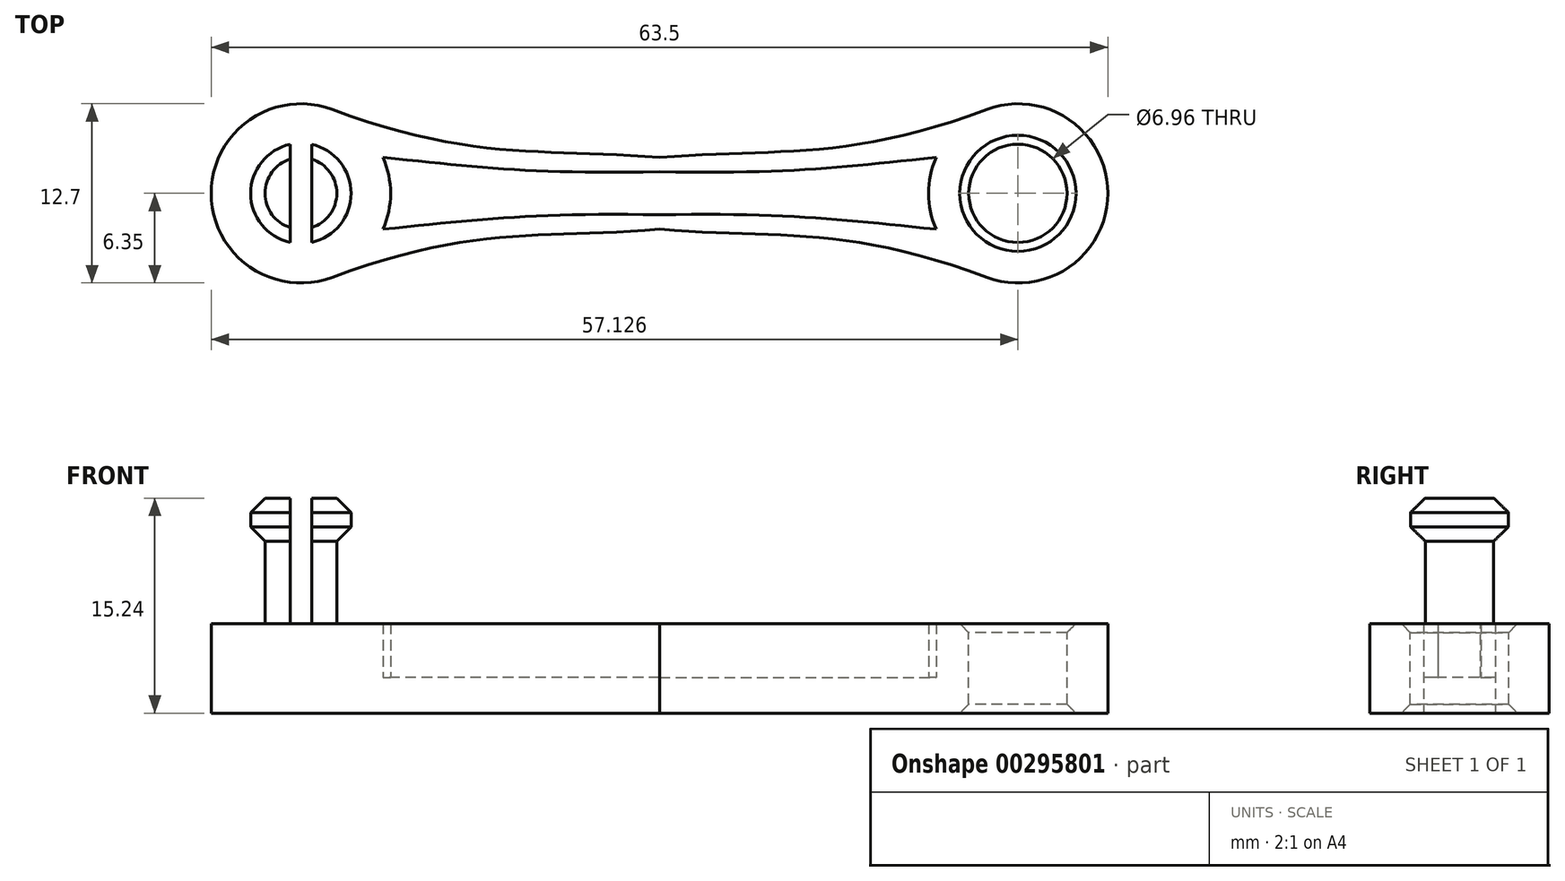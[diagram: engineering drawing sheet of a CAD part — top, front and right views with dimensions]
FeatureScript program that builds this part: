
annotation { "Feature Type Name" : "Feature", "Feature Type Description" : "" }
export const myFeature = defineFeature(function(context is Context, id is Id, definition is map)
    precondition{}
    {
        {
            var Q0;
            Q0=qCreatedBy(makeId("Top.planeOp"),FACE);
            var sketch = newSketch(context, id + "F0", { "sketchPlane" : qUnion([Q0])});
            skLineSegment(sketch, "E0.left", {"start": v(-25.42, 6.35) * mm, "end": v(-25.38, -6.35) * mm, "construction": true});
            skLineSegment(sketch, "E0.right", {"start": v(25.38, 6.35) * mm, "end": v(25.42, -6.35) * mm, "construction": true});
            skPoint(sketch, "E0.middle", {"position": v(0, 0) * mm});
            skCircle(sketch, "E1", {"center": v(-25.4, 0) * mm, "radius": 6.35 * mm});
            skCircle(sketch, "E2", {"center": v(25.4, 0) * mm, "radius": 6.35 * mm});
            skLineSegment(sketch, "E3", {"start": v(0, 0) * mm, "end": v(0, 1.52) * mm, "construction": true});
            skLineSegment(sketch, "E4", {"start": v(0, 1.52) * mm, "end": v(0, 2.54) * mm, "construction": true});
            skFitSpline(sketch, "E5", {"points": [v(0, 1.52) * mm, v(-19.58, 2.54) * mm], "startDerivative": vector(-27.23, -0.5) * mm, "endDerivative": vector(-20.14, 2.02) * mm});
            skFitSpline(sketch, "E6.MirrorCS", {"points": [v(0, 1.52) * mm, v(19.58, 2.54) * mm], "startDerivative": vector(27.23, -0.5) * mm, "endDerivative": vector(20.14, 2.02) * mm});
            skFitSpline(sketch, "E7.MirrorCS", {"points": [v(0, -1.52) * mm, v(19.58, -2.54) * mm], "startDerivative": vector(27.23, 0.5) * mm, "endDerivative": vector(20.14, -2.02) * mm});
            skFitSpline(sketch, "E8.MirrorCS", {"points": [v(0, -1.52) * mm, v(-19.58, -2.54) * mm], "startDerivative": vector(-27.23, 0.5) * mm, "endDerivative": vector(-20.14, -2.02) * mm});
            skFitSpline(sketch, "E9", {"points": [v(0, 2.54) * mm, v(-23.18, 5.95) * mm], "startDerivative": vector(-24.38, 2.12) * mm, "endDerivative": vector(-30.2, 11.29) * mm});
            skFitSpline(sketch, "E10.MirrorCS", {"points": [v(0, 2.54) * mm, v(23.18, 5.95) * mm], "startDerivative": vector(24.38, 2.12) * mm, "endDerivative": vector(30.2, 11.29) * mm});
            skFitSpline(sketch, "E11.MirrorCS", {"points": [v(0, -2.54) * mm, v(-23.18, -5.95) * mm], "startDerivative": vector(-24.38, -2.12) * mm, "endDerivative": vector(-30.2, -11.29) * mm});
            skFitSpline(sketch, "E12.MirrorCS", {"points": [v(0, -2.54) * mm, v(23.18, -5.95) * mm], "startDerivative": vector(24.38, -2.12) * mm, "endDerivative": vector(30.2, -11.29) * mm});
            skSolve(sketch);
        }
        {
            var Q0;
            Q0=qCreatedBy(makeId("Front.planeOp"),FACE);
            var sketch = newSketch(context, id + "F1", { "sketchPlane" : qUnion([Q0])});
            skPoint(sketch, "E13.0", {"position": v(25.38, 0) * mm});
            skLineSegment(sketch, "E14", {"start": v(25.38, 0) * mm, "end": v(25.38, 6.35) * mm});
            skLineSegment(sketch, "E15.bottom", {"start": v(28.86, 5.72) * mm, "end": v(21.9, 5.72) * mm, "construction": true});
            skLineSegment(sketch, "E15.top", {"start": v(28.86, 0.64) * mm, "end": v(21.9, 0.64) * mm, "construction": true});
            skLineSegment(sketch, "E15.left", {"start": v(28.86, 5.72) * mm, "end": v(28.86, 0.64) * mm});
            skLineSegment(sketch, "E15.right", {"start": v(21.9, 5.72) * mm, "end": v(21.9, 0.64) * mm});
            skPoint(sketch, "E15.middle", {"position": v(25.38, 3.18) * mm});
            skLineSegment(sketch, "E16.bottom", {"start": v(29.5, 0) * mm, "end": v(21.26, 0) * mm});
            skLineSegment(sketch, "E16.top", {"start": v(29.5, 6.35) * mm, "end": v(21.26, 6.35) * mm});
            skLineSegment(sketch, "E16.left", {"start": v(29.5, 0) * mm, "end": v(29.5, 6.35) * mm, "construction": true});
            skLineSegment(sketch, "E16.right", {"start": v(21.26, 0) * mm, "end": v(21.26, 6.35) * mm, "construction": true});
            skLineSegment(sketch, "E17", {"start": v(28.86, 5.72) * mm, "end": v(29.5, 6.35) * mm});
            skLineSegment(sketch, "E18", {"start": v(21.9, 5.72) * mm, "end": v(21.26, 6.35) * mm});
            skLineSegment(sketch, "E19", {"start": v(21.9, 0.64) * mm, "end": v(21.26, 0) * mm});
            skLineSegment(sketch, "E20", {"start": v(28.86, 0.64) * mm, "end": v(29.5, 0) * mm});
            skPoint(sketch, "E21.0", {"position": v(-25.4, 0) * mm});
            skLineSegment(sketch, "E22", {"start": v(-25.4, 0) * mm, "end": v(-25.4, 6.35) * mm, "construction": true});
            skLineSegment(sketch, "E23", {"start": v(-25.4, 6.35) * mm, "end": v(-25.4, 15.24) * mm});
            skLineSegment(sketch, "E24.bottom", {"start": v(-22.86, 15.24) * mm, "end": v(-27.94, 15.24) * mm});
            skLineSegment(sketch, "E24.top", {"start": v(-22.86, 6.35) * mm, "end": v(-27.94, 6.35) * mm});
            skLineSegment(sketch, "E24.left", {"start": v(-22.86, 15.24) * mm, "end": v(-22.86, 6.35) * mm});
            skLineSegment(sketch, "E24.right", {"start": v(-27.94, 15.24) * mm, "end": v(-27.94, 6.35) * mm});
            skPoint(sketch, "E24.middle", {"position": v(-25.4, 10.8) * mm});
            skLineSegment(sketch, "E25.bottom", {"start": v(-21.84, 15.24) * mm, "end": v(-28.96, 15.24) * mm});
            skLineSegment(sketch, "E25.top", {"start": v(-21.84, 12.2) * mm, "end": v(-28.96, 12.2) * mm});
            skLineSegment(sketch, "E25.left", {"start": v(-21.84, 15.24) * mm, "end": v(-21.84, 12.2) * mm});
            skLineSegment(sketch, "E25.right", {"start": v(-28.96, 15.24) * mm, "end": v(-28.96, 12.2) * mm});
            skPoint(sketch, "E25.middle", {"position": v(-25.4, 13.72) * mm});
            skLineSegment(sketch, "E26", {"start": v(-21.84, 14.22) * mm, "end": v(-22.86, 15.24) * mm});
            skLineSegment(sketch, "E27", {"start": v(-21.84, 13.2) * mm, "end": v(-22.86, 12.2) * mm});
            skLineSegment(sketch, "E28", {"start": v(-27.94, 15.24) * mm, "end": v(-28.96, 14.22) * mm});
            skLineSegment(sketch, "E29", {"start": v(-27.94, 12.2) * mm, "end": v(-28.96, 13.2) * mm});
            skLineSegment(sketch, "E30.bottom", {"start": v(-24.64, 15.24) * mm, "end": v(-26.16, 15.24) * mm});
            skLineSegment(sketch, "E30.top", {"start": v(-24.64, 6.35) * mm, "end": v(-26.16, 6.35) * mm});
            skLineSegment(sketch, "E30.left", {"start": v(-24.64, 15.24) * mm, "end": v(-24.64, 6.35) * mm});
            skLineSegment(sketch, "E30.right", {"start": v(-26.16, 15.24) * mm, "end": v(-26.16, 6.35) * mm});
            skSolve(sketch);
        }
        {
            var Q0;
            {var subQ0=sQuery(id+"F0.wireOp",EDGE,"E2");var subQ1=makeQuery(id+"F0.imprint","INTERSECT",VERTEX,{"derivedFrom":[sQuery(id+"F0.wireOp",EDGE,"E0.bottom"),subQ0]});Q0=makeQuery(id+"F0.imprint","IMPRINT",FACE,{"disambiguationData":[TD([[makeQuery(id+"F0.imprint","IMPRINT",EDGE,{"disambiguationData":[TD([[subQ1,-1.0]])],"derivedFrom":subQ0}),1.0]])]});}
            var Q1;
            {var subQ0=sQuery(id+"F0.wireOp",EDGE,"E1");var subQ1=makeQuery(id+"F0.imprint","INTERSECT",VERTEX,{"derivedFrom":[sQuery(id+"F0.wireOp",EDGE,"E0.bottom"),subQ0]});Q1=makeQuery(id+"F0.imprint","IMPRINT",FACE,{"disambiguationData":[TD([[makeQuery(id+"F0.imprint","IMPRINT",EDGE,{"disambiguationData":[TD([[subQ1,-1.0]])],"derivedFrom":subQ0}),1.0]])]});}
            var Q2;
            {var subQ8=sQuery(id+"F0.wireOp",EDGE,"E5");Q2=makeQuery(id+"F0.imprint","IMPRINT",FACE,{"disambiguationData":[TD([[makeQuery(id+"F0.imprint","IMPRINT",EDGE,{"derivedFrom":subQ8}),-1.0]])]});}
            var Q3;
            {var subQ7=sQuery(id+"F0.wireOp",EDGE,"E7.MirrorCS");Q3=makeQuery(id+"F0.imprint","IMPRINT",FACE,{"disambiguationData":[TD([[makeQuery(id+"F0.imprint","IMPRINT",EDGE,{"derivedFrom":subQ7}),-1.0]])]});}
            extrude(context, id + "F2", {"entities" : qUnion([Q0, Q1, Q2, Q3]), "depth" : 6.35 * mm});
        }
        {
            var Q0;
            {var subQ1=sQuery(id+"F1.wireOp",EDGE,"E14");Q0=makeQuery(id+"F1.imprint","IMPRINT",FACE,{"disambiguationData":[TD([[makeQuery(id+"F1.imprint","IMPRINT",EDGE,{"derivedFrom":subQ1}),-1.0]])]});}
            var Q1;
            Q1=sQuery(id+"F1.wireOp",EDGE,"E14");
            revolve(context, id + "F3", {"operationType" : NewBodyOperationType.REMOVE, "entities" : qUnion([Q0]), "axis" : qUnion([Q1]), "revolveType" : RevolveType.FULL, "oppositeDirection" : true});
        }
        {
            var Q0;
            {var subQ0=sQuery(id+"F1.wireOp",EDGE,"E26");Q0=makeQuery(id+"F1.imprint","IMPRINT",FACE,{"disambiguationData":[TD([[makeQuery(id+"F1.imprint","IMPRINT",EDGE,{"derivedFrom":subQ0}),1.0]])]});}
            var Q1;
            {var subQ3=sQuery(id+"F1.wireOp",EDGE,"E25.top");var subQ5=sQuery(id+"F1.wireOp",EDGE,"E30.left");var subQ7=makeQuery(id+"F1.imprint","INTERSECT",VERTEX,{"derivedFrom":[subQ3,subQ5]});Q1=makeQuery(id+"F1.imprint","IMPRINT",FACE,{"disambiguationData":[TD([[makeQuery(id+"F1.imprint","IMPRINT",EDGE,{"disambiguationData":[TD([[subQ7,1.0]])],"derivedFrom":subQ3}),-1.0]])]});}
            var Q2;
            {var subQ3=sQuery(id+"F1.wireOp",EDGE,"E25.top");var subQ5=sQuery(id+"F1.wireOp",EDGE,"E30.right");var subQ6=makeQuery(id+"F1.imprint","INTERSECT",VERTEX,{"derivedFrom":[subQ3,subQ5]});Q2=makeQuery(id+"F1.imprint","IMPRINT",FACE,{"disambiguationData":[TD([[makeQuery(id+"F1.imprint","IMPRINT",EDGE,{"disambiguationData":[TD([[subQ6,-1.0]])],"derivedFrom":subQ3}),-1.0]])]});}
            var Q3;
            {var subQ0=sQuery(id+"F1.wireOp",EDGE,"E28");Q3=makeQuery(id+"F1.imprint","IMPRINT",FACE,{"disambiguationData":[TD([[makeQuery(id+"F1.imprint","IMPRINT",EDGE,{"derivedFrom":subQ0}),1.0]])]});}
            var Q4;
            {var subQ0=sQuery(id+"F1.wireOp",EDGE,"E24.right");var subQ1=sQuery(id+"F1.wireOp",EDGE,"E24.top");var subQ2=makeQuery(id+"F1.imprint","INTERSECT",VERTEX,{"derivedFrom":[subQ1,subQ0]});Q4=makeQuery(id+"F1.imprint","IMPRINT",FACE,{"disambiguationData":[TD([[makeQuery(id+"F1.imprint","IMPRINT",EDGE,{"disambiguationData":[TD([[subQ2,1.0]])],"derivedFrom":subQ1}),-1.0]])]});}
            var Q5;
            {var subQ0=sQuery(id+"F1.wireOp",EDGE,"E24.left");var subQ1=sQuery(id+"F1.wireOp",EDGE,"E24.top");var subQ2=makeQuery(id+"F1.imprint","INTERSECT",VERTEX,{"derivedFrom":[subQ1,subQ0]});Q5=makeQuery(id+"F1.imprint","IMPRINT",FACE,{"disambiguationData":[TD([[makeQuery(id+"F1.imprint","IMPRINT",EDGE,{"disambiguationData":[TD([[subQ2,-1.0]])],"derivedFrom":subQ1}),-1.0]])]});}
            var Q6;
            Q6=sQuery(id+"F1.wireOp",EDGE,"E23");
            revolve(context, id + "F4", {"operationType" : NewBodyOperationType.ADD, "entities" : qUnion([Q0, Q1, Q2, Q3, Q4, Q5]), "axis" : qUnion([Q6]), "revolveType" : RevolveType.FULL});
        }
        {
            var Q0;
            {var subQ0=sQuery(id+"F1.wireOp",EDGE,"E30.bottom");var subQ1=sQuery(id+"F1.wireOp",EDGE,"E23");var subQ2=makeQuery(id+"F1.imprint","INTERSECT",VERTEX,{"derivedFrom":[subQ1,subQ0]});Q0=makeQuery(id+"F1.imprint","IMPRINT",FACE,{"disambiguationData":[TD([[makeQuery(id+"F1.imprint","IMPRINT",EDGE,{"disambiguationData":[TD([[subQ2,1.0]])],"derivedFrom":subQ1}),-1.0]])]});}
            var Q1;
            {var subQ0=sQuery(id+"F1.wireOp",EDGE,"E30.bottom");var subQ1=sQuery(id+"F1.wireOp",EDGE,"E23");var subQ2=makeQuery(id+"F1.imprint","INTERSECT",VERTEX,{"derivedFrom":[subQ1,subQ0]});Q1=makeQuery(id+"F1.imprint","IMPRINT",FACE,{"disambiguationData":[TD([[makeQuery(id+"F1.imprint","IMPRINT",EDGE,{"disambiguationData":[TD([[subQ2,1.0]])],"derivedFrom":subQ1}),1.0]])]});}
            var Q2;
            {var subQ0=sQuery(id+"F1.wireOp",EDGE,"E30.top");var subQ1=sQuery(id+"F1.wireOp",EDGE,"E23");var subQ2=makeQuery(id+"F1.imprint","INTERSECT",VERTEX,{"derivedFrom":[subQ1,subQ0]});Q2=makeQuery(id+"F1.imprint","IMPRINT",FACE,{"disambiguationData":[TD([[makeQuery(id+"F1.imprint","IMPRINT",EDGE,{"disambiguationData":[TD([[subQ2,-1.0]])],"derivedFrom":subQ1}),-1.0]])]});}
            var Q3;
            {var subQ0=sQuery(id+"F1.wireOp",EDGE,"E30.top");var subQ1=sQuery(id+"F1.wireOp",EDGE,"E23");var subQ2=makeQuery(id+"F1.imprint","INTERSECT",VERTEX,{"derivedFrom":[subQ1,subQ0]});Q3=makeQuery(id+"F1.imprint","IMPRINT",FACE,{"disambiguationData":[TD([[makeQuery(id+"F1.imprint","IMPRINT",EDGE,{"disambiguationData":[TD([[subQ2,-1.0]])],"derivedFrom":subQ1}),1.0]])]});}
            extrude(context, id + "F5", {"entities" : qUnion([Q0, Q1, Q2, Q3]), "operationType" : NewBodyOperationType.REMOVE, "endBound" : BoundingType.SYMMETRIC, "depth" : 25.4 * mm});
        }
        {
            var Q0;
            {var subQ1=sQuery(id+"F0.wireOp",EDGE,"E5");Q0=makeQuery(id+"F0.imprint","IMPRINT",FACE,{"disambiguationData":[TD([[makeQuery(id+"F0.imprint","IMPRINT",EDGE,{"derivedFrom":subQ1}),1.0]])]});}
            extrude(context, id + "F6", {"entities" : qUnion([Q0]), "operationType" : NewBodyOperationType.ADD, "depth" : 2.54 * mm});
        }
    });
